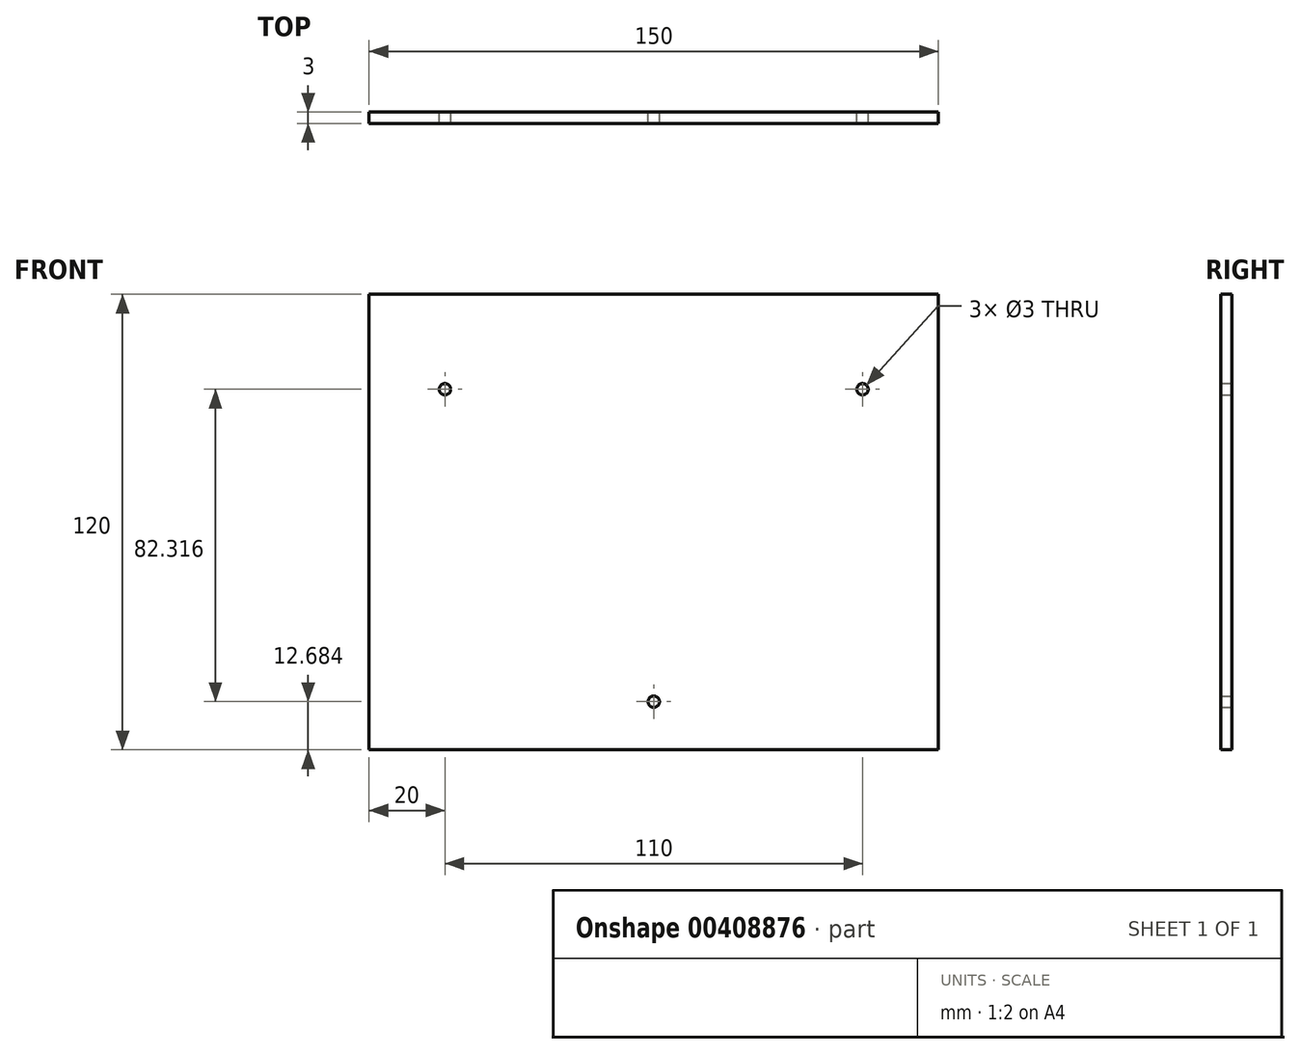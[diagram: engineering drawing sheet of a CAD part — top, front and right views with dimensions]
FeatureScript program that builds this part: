
annotation { "Feature Type Name" : "Feature", "Feature Type Description" : "" }
export const myFeature = defineFeature(function(context is Context, id is Id, definition is map)
    precondition{}
    {
        {
            var Q0;
            Q0=qCreatedBy(makeId("Front.planeOp"),FACE);
            var sketch = newSketch(context, id + "F0", { "sketchPlane" : qUnion([Q0])});
            skLineSegment(sketch, "E0.bottom", {"start": v(75, -60) * mm, "end": v(-75, -60) * mm});
            skLineSegment(sketch, "E0.top", {"start": v(75, 60) * mm, "end": v(-75, 60) * mm});
            skLineSegment(sketch, "E0.left", {"start": v(75, -60) * mm, "end": v(75, 60) * mm});
            skLineSegment(sketch, "E0.right", {"start": v(-75, -60) * mm, "end": v(-75, 60) * mm});
            skPoint(sketch, "E0.middle", {"position": v(0, 0) * mm});
            skCircle(sketch, "E1", {"center": v(-55, 35) * mm, "radius": 1.5 * mm});
            skCircle(sketch, "E2", {"center": v(55, 35) * mm, "radius": 1.5 * mm});
            skCircle(sketch, "E3", {"center": v(0, -47.32) * mm, "radius": 1.5 * mm});
            skSolve(sketch);
        }
        {
            var Q0;
            Q0=makeQuery(id+"F0.imprint","IMPRINT",FACE,{"disambiguationData":[TD([[makeQuery(id+"F0.imprint","IMPRINT",EDGE,{"derivedFrom":sQuery(id+"F0.wireOp",EDGE,"E0.bottom")}),-1.0]])]});
            extrude(context, id + "F1", {"entities" : qUnion([Q0]), "depth" : 3 * mm});
        }
    });
